# Revit family: P810027-020-30
name_source: partatom
category: Lighting Fixtures
revit_build: Autodesk Revit 2014 (Build: 20130308_1515(x64)
units: mm (PartAtom-declared; Revit-internal decimal feet)

## types (1)
- P810027-020-30
    Apparent Load = 13 VA
    Assembly Code = D5020200
    Color Filter = 16777215
    Connector Description = Lighting Connector
    Default Elevation = 48 "
    Description = Revel in the brilliant combination of easy installation and a sleek, modern
lighting aesthetic offered by our Emblem Surface Mount LED Collection. A
symbol of clean, classic designs with smooth, eye-appealing curvature, Emblem provides you with familiar lighting shapes and functional features
engineered for both outstanding performance and unparalleled longevity. An
excellent choice for general ambient lighting, each polished design features a
smooth, slightly tapered trim ring surrounding a single, integrated LED light
source. Each trim ring is available in two different sizes and finishes to help
meet your unique design needs. Enjoy the unmatched level of glare control offered by the fixture’s diffused polycarbonate lens that also hides any
unwanted LED pixilation. Each light fixture is home to an integrated AC LED
light engine that seamlessly installs to a variety of ceiling pan junction boxes
to give you added flexibility when it comes to creating your design vision.
The surface mount will also satiate the cravings of any environmentally-aware
and cost-savvy buyer with the fixture’s long-lasting, 50,000-hour LED life
span and 80% energy savings.
    Dimming Lamp Color Temperature Shift = <None>
    Features = • Diffused polycarbonate lens
• Integrated AC LED technology 3000K, 90 CRI, 750 lumens (delivered)
• Die-cast aluminum construction with a powder coat paint finish
• Diffused polycarbonate lens controls direct glare from the LEDs
• Lumen output and distribution comparable to a 65W incandescent lamp
• Dimmable to 10% brightness with many Electronic Low Voltage (ELV) & Forward Phase
(TRIAC) dimmers
• Bronze Finish
• CSA Listed for Wet Location applications
• Fixture installs to 4” Octagon metallic junction boxes, 4” Round non-metallic junction boxes
and 4” x 1/2” round ceiling pan junction box.
• 50,000 hour rated lifetime
• Dimmable to 10% brightness (See Dimming Notes)
• Mounting strap for outlet box included
• 6 in of wire supplied
    Fixture distribution = Direct
    Glass = Paint - Hubbell - White Texture
    Height = 15 "
    Housing Material = Paint - Hubbell - Textured Camera Black
    Lamp = LED
    Load Classification = Lighting
    Manufacturer = Progress Lighting
    Model = P810027-020-30
    Photometric Web File = generic.ies
    Power Factor = 1
    Product Documentation Link = https://hubbellcdn.com
    Product Link = https://www.hubbell.com
    Tilt Angle = -90.00°
    URL = https://www.hubbell.com
    Voltage = 120 V
    Warranty = 5 years Warranty
    Wattage Comments = 12.5W
    Watts = 13 W
    Width = 5.5 "

## geometry (parser evidence)
native form markers: Sweep x4
no freeform markers — native parametric forms only
